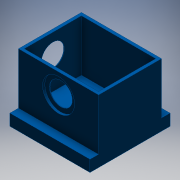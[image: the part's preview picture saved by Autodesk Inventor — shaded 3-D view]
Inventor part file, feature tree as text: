
AUTODESK INVENTOR PART (.ipt)
format: ipt  version: 2016 (Build 200138000, 138)  size: 169,472 bytes
history: native  units: mm
features: extrude x6, sketch x6
ambient origin geometry x8: Origin, YZ Plane, XZ Plane, XY Plane, X Axis, Y Axis, Z Axis, Center Point
bodies: Solid1 (feature_tree)
feature tree (12):
  extrude  "Extrusion1"  Depth=70.0mm
  extrude  "Extrusion2"  Depth=70.0mm
  extrude  "Extrusion8"  Depth=70.0mm
  extrude  "Extrusion9"  Depth=55.0mm
  extrude  "Extrusion12"  Depth=2.5mm
  extrude  "Extrusion13"  Depth=2.5mm
  sketch  "Sketch1"  dims[d0=70.0mm d1=35.0mm]
  sketch  "Sketch3"  dims[d2=70.0mm d3=35.0mm]
  sketch  "Sketch9"  dims[d4=10.0mm d5=0.0mm d17=70.0mm]
  sketch  "Sketch10"  dims[d18=55.0mm d19=27.5mm]
  sketch  "Sketch13"  dims[d20=2.5mm d21=2.5mm]
  sketch  "Sketch14"  dims[d22=2.5mm d23=2.5mm d24=45.0mm d25=0.0mm d60=28.0mm d61=35.0mm d62=27.5mm d63=2.0mm d64=0.0mm d65=20.0mm d66=2.0mm d67=0.0mm d76=28.0mm d78=2.0mm d79=0.0mm d80=20.0mm d81=27.5mm d82=27.5mm d83=2.0mm d84=0.0mm]
